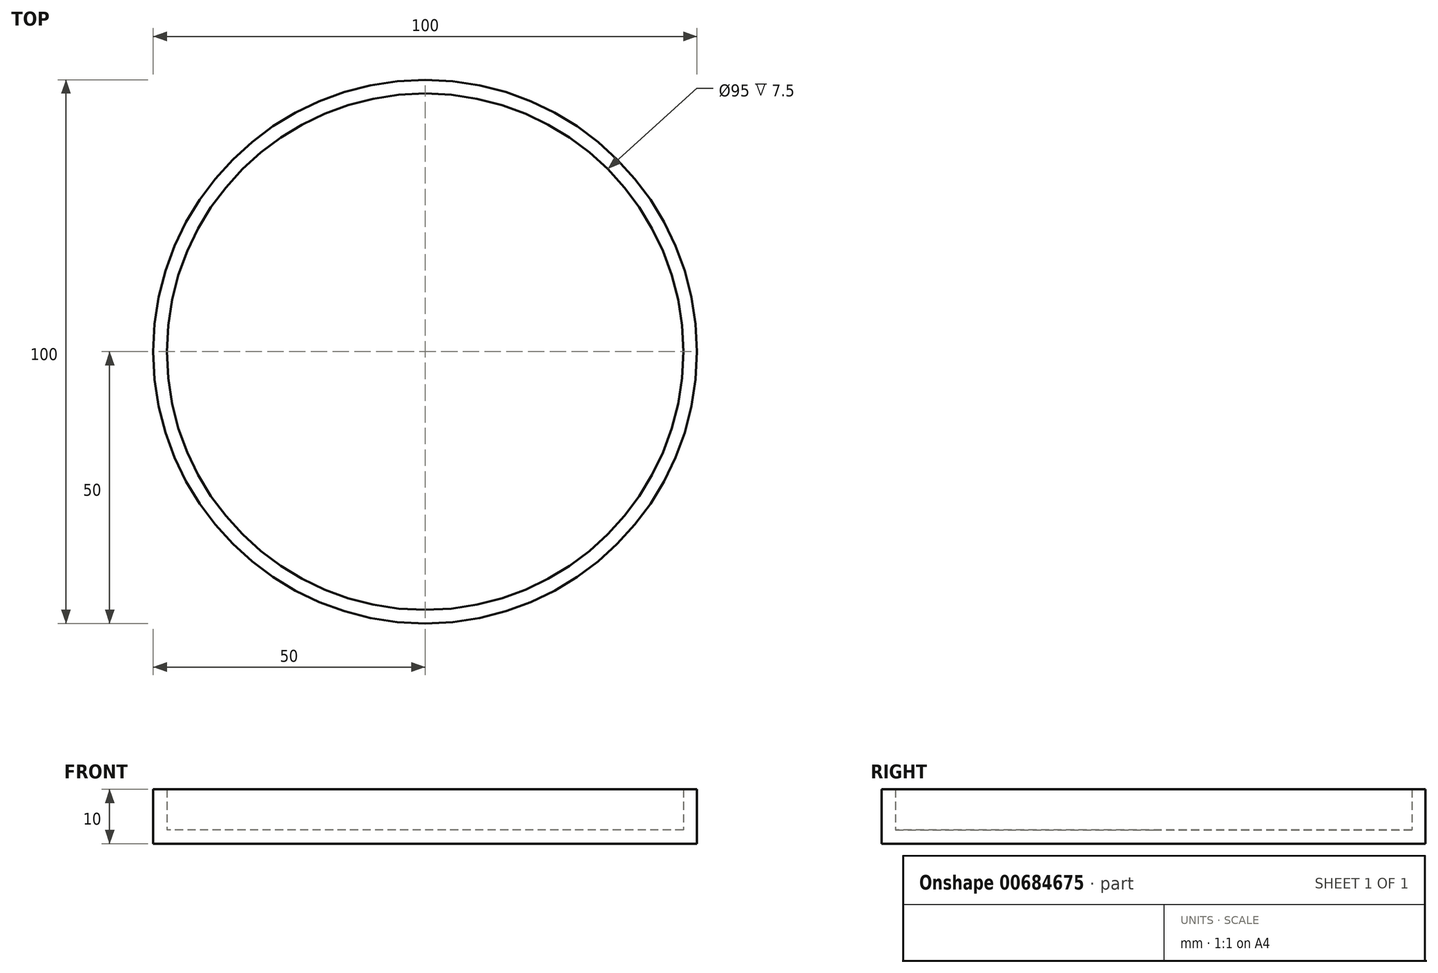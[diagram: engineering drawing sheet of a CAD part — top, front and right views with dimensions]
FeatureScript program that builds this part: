
annotation { "Feature Type Name" : "Feature", "Feature Type Description" : "" }
export const myFeature = defineFeature(function(context is Context, id is Id, definition is map)
    precondition{}
    {
        {
            var Q0;
            Q0=qCreatedBy(makeId("Top.planeOp"),FACE);
            var sketch = newSketch(context, id + "F0", { "sketchPlane" : qUnion([Q0])});
            skCircle(sketch, "E0", {"center": v(0, 0) * mm, "radius": 50 * mm});
            skCircle(sketch, "E1.0", {"center": v(0, 0) * mm, "radius": 45 * mm});
            skSolve(sketch);
        }
        {
            var Q0;
            Q0=makeQuery(id+"F0.imprint","IMPRINT",FACE,{"disambiguationData":[TD([[makeQuery(id+"F0.imprint","IMPRINT",EDGE,{"derivedFrom":sQuery(id+"F0.wireOp",EDGE,"E0")}),1.0]])]});
            var Q1;
            Q1=makeQuery(id+"F0.imprint","IMPRINT",FACE,{"disambiguationData":[TD([[makeQuery(id+"F0.imprint","IMPRINT",EDGE,{"derivedFrom":sQuery(id+"F0.wireOp",EDGE,"E1.0")}),1.0]])]});
            extrude(context, id + "F1", {"entities" : qUnion([Q0, Q1]), "depth" : 10 * mm, "offsetDistance" : 25 * mm});
        }
        {
            var Q0;
            Q0=makeQuery(id+"F1.opExtrude","CAP_FACE",FACE,{"disambiguationData":[OSD([sQuery(id+"F0.wireOp",EDGE,"E0")])],"isStart":false});
            shell(context, id + "F2", {"entities" : qUnion([Q0]), "thickness" : 2.5 * mm});
        }
    });
